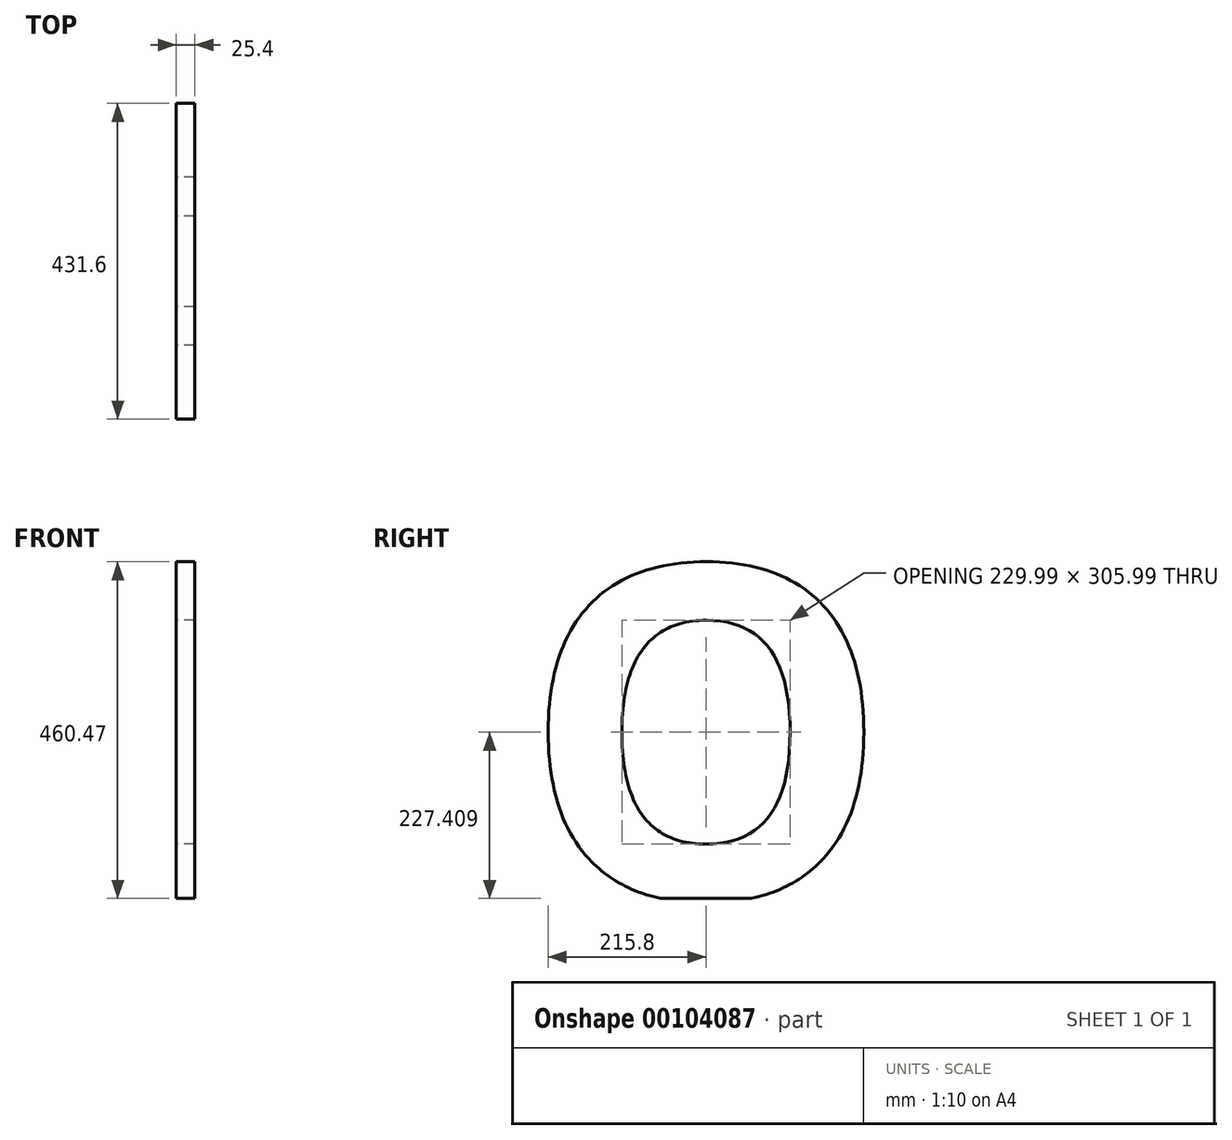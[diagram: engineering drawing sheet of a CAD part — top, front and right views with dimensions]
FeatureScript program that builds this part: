
annotation { "Feature Type Name" : "Feature", "Feature Type Description" : "" }
export const myFeature = defineFeature(function(context is Context, id is Id, definition is map)
    precondition{}
    {
        {
            var Q0;
            Q0=qCreatedBy(makeId("Right.planeOp"),FACE);
            var sketch = newSketch(context, id + "F0", { "sketchPlane" : qUnion([Q0])});
            skText(sketch, "E0", { "text": "O", "fontName": "OpenSans-Bold.ttf"});
            const initialGuessF0  = {"E0": [-0.16492, -0.26902, 1, 0, 0.4572]};
            skSetInitialGuess(sketch, initialGuessF0);
            skSolve(sketch);
        }
        {
            var Q0;
            Q0 = qSketchRegion(id + "F0", true);
            extrude(context, id + "F1", {"entities" : qUnion([Q0]), "endBound" : BoundingType.SYMMETRIC, "depth" : 25.4 * mm});
        }
        {
            var Q0;
            Q0=makeQuery(id+"F1.opExtrude","CAP_FACE",FACE,{"disambiguationData":[OSD([sQuery(id+"F0.wireOp",EDGE,"E0.sketch_text.stroke-0"),sQuery(id+"F0.wireOp",EDGE,"E0.sketch_text.stroke-1"),sQuery(id+"F0.wireOp",EDGE,"E0.sketch_text.stroke-2"),sQuery(id+"F0.wireOp",EDGE,"E0.sketch_text.stroke-3"),sQuery(id+"F0.wireOp",EDGE,"E0.sketch_text.stroke-4"),sQuery(id+"F0.wireOp",EDGE,"E0.sketch_text.stroke-5"),sQuery(id+"F0.wireOp",EDGE,"E0.sketch_text.stroke-6"),sQuery(id+"F0.wireOp",EDGE,"E0.sketch_text.stroke-7"),sQuery(id+"F0.wireOp",EDGE,"E0.sketch_text.stroke-8"),sQuery(id+"F0.wireOp",EDGE,"E0.sketch_text.stroke-9"),sQuery(id+"F0.wireOp",EDGE,"E0.sketch_text.stroke-10"),sQuery(id+"F0.wireOp",EDGE,"E0.sketch_text.stroke-11"),sQuery(id+"F0.wireOp",EDGE,"E0.sketch_text.stroke-12"),sQuery(id+"F0.wireOp",EDGE,"E0.sketch_text.stroke-13")])],"isStart":false});
            var sketch = newSketch(context, id + "F2", { "sketchPlane" : qUnion([Q0])});
            skLineSegment(sketch, "E1.0", {"start": v(-164.92, -269.02) * mm, "end": v(303.6, -269.02) * mm, "construction": true});
            skLineSegment(sketch, "E2.bottom", {"start": v(-164.92, -269.02) * mm, "end": v(291.65, -269.02) * mm});
            skLineSegment(sketch, "E2.top", {"start": v(-164.92, -347.5) * mm, "end": v(291.65, -347.5) * mm});
            skLineSegment(sketch, "E2.left", {"start": v(-164.92, -269.02) * mm, "end": v(-164.92, -347.5) * mm});
            skLineSegment(sketch, "E2.right", {"start": v(291.65, -269.02) * mm, "end": v(291.65, -347.5) * mm});
            skSolve(sketch);
        }
        {
            var Q0;
            Q0 = qSketchRegion(id + "F2", true);
            extrude(context, id + "F3", {"entities" : qUnion([Q0]), "operationType" : NewBodyOperationType.REMOVE, "endBound" : BoundingType.THROUGH_ALL, "oppositeDirection" : true, "depth" : 25.4 * mm});
        }
    });
